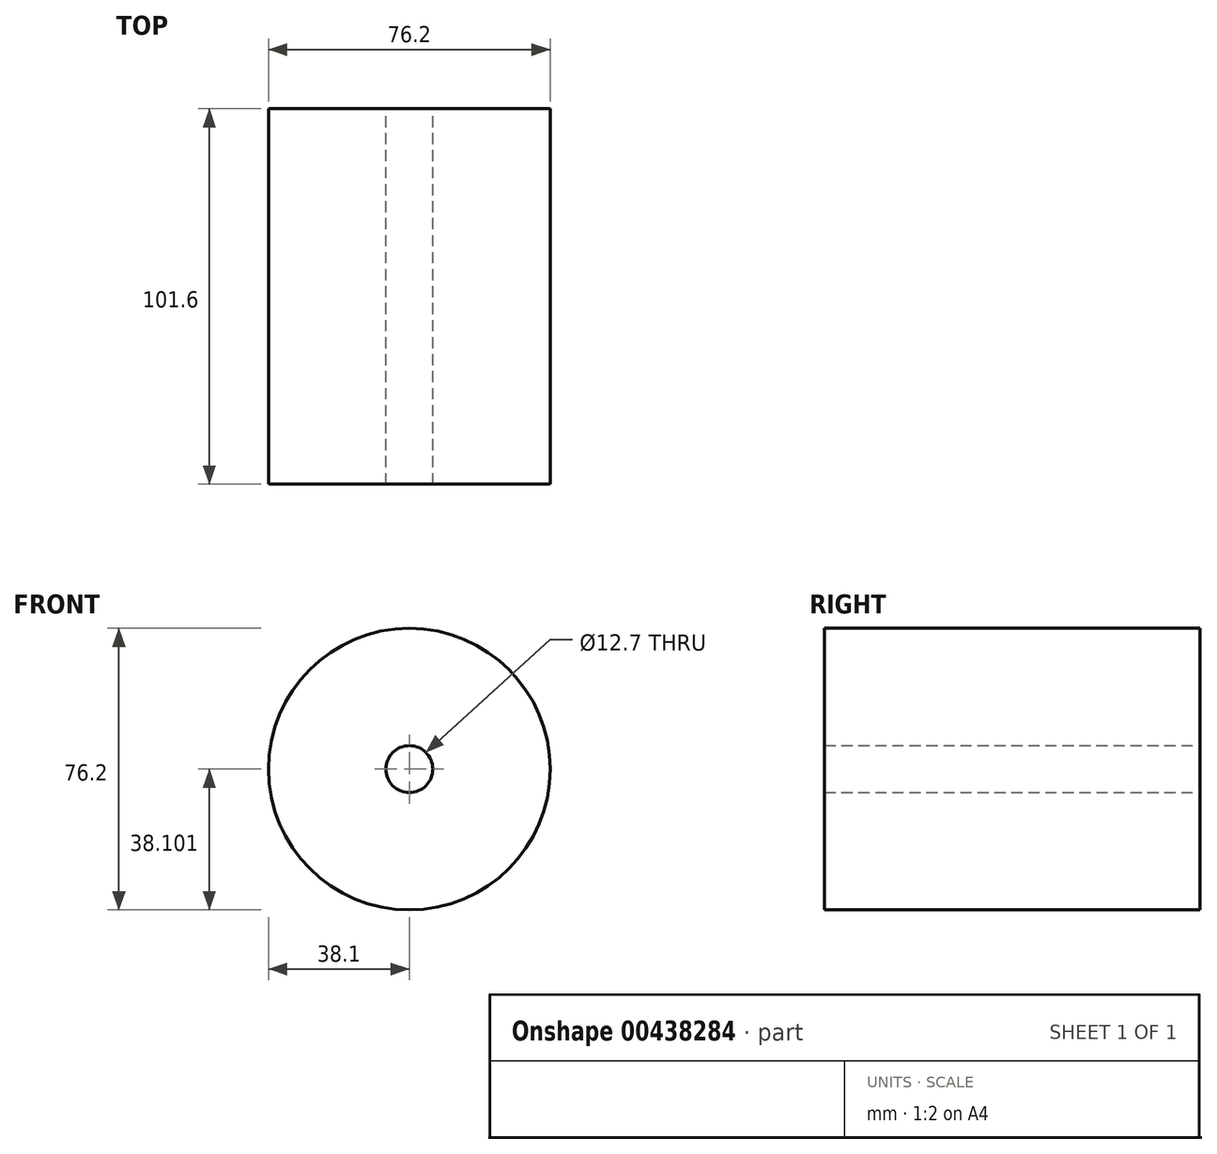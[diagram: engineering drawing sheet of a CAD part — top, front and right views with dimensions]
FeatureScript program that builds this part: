
annotation { "Feature Type Name" : "Feature", "Feature Type Description" : "" }
export const myFeature = defineFeature(function(context is Context, id is Id, definition is map)
    precondition{}
    {
        {
            var Q0;
            Q0=qCreatedBy(makeId("Front.planeOp"),FACE);
            var sketch = newSketch(context, id + "F0", { "sketchPlane" : qUnion([Q0])});
            skCircle(sketch, "E0", {"center": v(0, 37.8) * mm, "radius": 38.1 * mm});
            skCircle(sketch, "E1.0", {"center": v(0, 37.8) * mm, "radius": 6.35 * mm});
            skSolve(sketch);
        }
        {
            var Q0;
            Q0=makeQuery(id+"F0.imprint","IMPRINT",FACE,{"disambiguationData":[TD([[makeQuery(id+"F0.imprint","IMPRINT",EDGE,{"derivedFrom":sQuery(id+"F0.wireOp",EDGE,"E0")}),1.0]])]});
            extrude(context, id + "F1", {"entities" : qUnion([Q0]), "depth" : 101.6 * mm});
        }
    });
